# Revit family: VLN_Nim-II-Mes-E_Multiproduct_BIM_NL_F3046;F3047
name_source: partatom
category: Plumbing Fixtures
revit_build: Autodesk Revit MEP 2014 (Build: 20130308_1515(x64)
units: mm (PartAtom-declared; Revit-internal decimal feet)

## types (2) — shared parameters
AreaUnits = millimeters
Assembly Code = C1030200
BREEAMApproved = No
Default Elevation = 800 mm  [stored 2.62467 ft]
ECA = No
IfcExportAs = IfcValveType
IfcExportType = FAUCET
LinearUnits = millimeters
NBSDescription = Water supply fittings for wash basins and troughs
NBSReference = 45-35-70/371
NominalHeight = 91 mm
NominalLength = 127 mm
NominalWidth = 47 mm  [stored 0.154199 ft]
Size = 47 x 127 x 91 mm
TMV3 = Yes
TestPressure = 10 Bar
URL = www.idealstandardnederland.nl
Uniclass2015Code = Pr_40_20_87_98
Uniclass2015Title = Washbasin taps
Uniclass2015Version = Products v1.1
Version = 1
VolumeUnits = liter
WRAS = No
WarrantyDescription = Fabrieksgarantie
WarrantyDurationUnit = jaar
WaterEfficientProduct = No
zero-valued in all types: CWFU, Cost, HWFU, WFU

## per-type parameters (varying)
- F3046AA - NIM-II-MES-E TOILETKRAAN CHR: Accessories=www.idealstandardnederland.nl; AssetType=Vast; BIMObjectName=VLN_Venlo_WashbasinTaps_F3046AA; BarCode=8711678062840; Brand=Venlo; CodePerformance=EN 817, DIN 4109; Color=Chroom; ConnectionType=Sanitair; Description=Venlo Nimbus II Messing toiletkraan eco. Koud. Vaste uitloop. Straalregelaar. Sprong 90 mm. Hoogte uitloop 38 mm. Eco bovendeel. Koppeling 12 mm.; DurationUnit=jaar; ExpectedLife=25; FaucetFunction=Toiletkraan; FaucetOperation=Eengreeps; FaucetType=Toiletkraan; Features=Toiletkraan eco. Koud. Vaste uitloop. Straalregelaar. Sprong 90 mm. Hoogte uitloop 38 mm. Eco bovendeel. Koppeling 12 mm.; Finish=Chroom; FlowRate=8,2 liter @ 3 bar; InstallationInstructions=http://www.idealstandardnederland.nl; ManufacturerURL=www.idealstandardnederland.nl; Material=Messing; Model=F3046AA; ModelNumber=F3046AA; ModelReference=Venlo Nimbus II Messing toiletkraan eco. Koud. Vaste uitloop. Straalregelaar. Sprong 90 mm. Hoogte uitloop 38 mm. Eco bovendeel. Koppeling 12 mm.; Name=WashbasinTaps_F3046AA_Venlo; NettWeight=0.621 kg; ProductInformation=http://www.idealstandardnederland.nl; Shape=Gesculptuurd; Space=Internal; SpareParts=www.idealstandardnederland.nl; ValveMechanism=Keramische schijven; ValveOperation=Eengreeps; WarrantyDurationParts=10; WorkingPressure=1-5 bar
- F3047AA - NIM-II-MES-E TOILETKRAAN CHR 5L/MIN: BIMObjectName=ISI_IdealStandard_WashbasinTaps_F3048AA; Brand=Ideal Standard; Model=F3048AA; ModelNumber=F3048AA; Name=WashbasinTaps_F3048AA_IdealStandard

note: [stored X ft] marks values corroborated as IEEE doubles in the binary element streams (Revit-internal decimal feet)

## geometry (parser evidence)
native form markers: Sweep x1
no freeform markers — native parametric forms only
